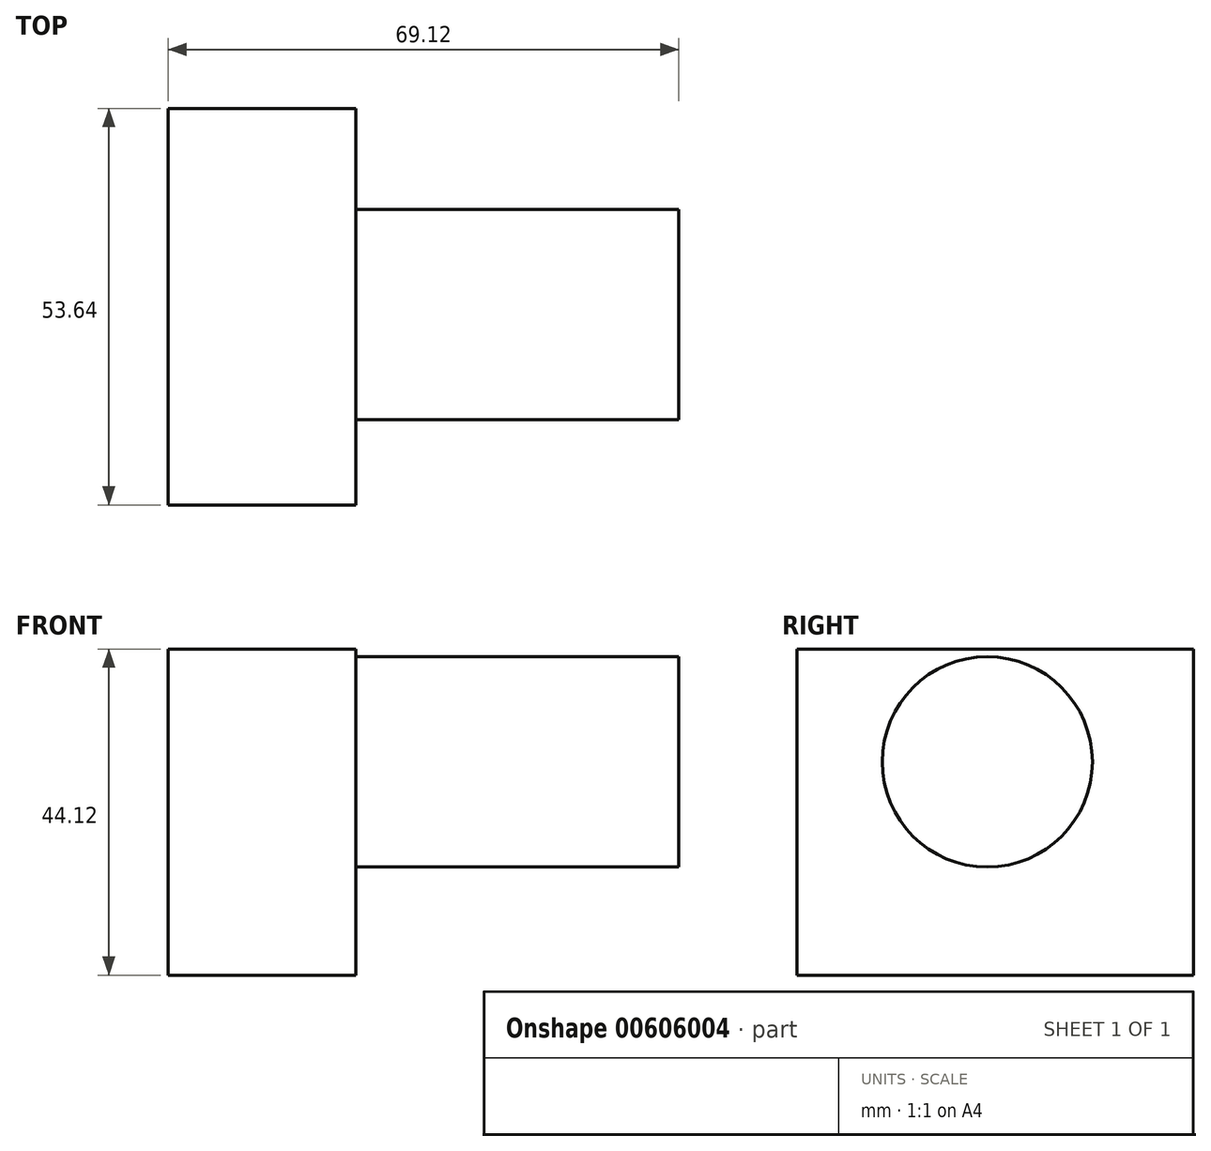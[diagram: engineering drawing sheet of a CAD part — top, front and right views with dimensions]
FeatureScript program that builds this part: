
annotation { "Feature Type Name" : "Feature", "Feature Type Description" : "" }
export const myFeature = defineFeature(function(context is Context, id is Id, definition is map)
    precondition{}
    {
        {
            var Q0;
            Q0=qCreatedBy(makeId("Right.planeOp"),FACE);
            var sketch = newSketch(context, id + "F0", { "sketchPlane" : qUnion([Q0])});
            skLineSegment(sketch, "E0.bottom", {"start": v(-35.96, 0) * mm, "end": v(17.68, 0) * mm});
            skLineSegment(sketch, "E0.top", {"start": v(-35.96, -44.12) * mm, "end": v(17.68, -44.12) * mm});
            skLineSegment(sketch, "E0.left", {"start": v(-35.96, 0) * mm, "end": v(-35.96, -44.12) * mm});
            skLineSegment(sketch, "E0.right", {"start": v(17.68, 0) * mm, "end": v(17.68, -44.12) * mm});
            skSolve(sketch);
        }
        {
            var Q0;
            Q0=makeQuery(id+"F0.imprint","IMPRINT",FACE,{"disambiguationData":[TD([[makeQuery(id+"F0.imprint","IMPRINT",EDGE,{"derivedFrom":sQuery(id+"F0.wireOp",EDGE,"E0.bottom")}),-1.0]])]});
            extrude(context, id + "F1", {"entities" : qUnion([Q0]), "depth" : 25.4 * mm, "offsetDistance" : 25.4 * mm});
        }
        {
            var Q0;
            Q0=makeQuery(id+"F1.opExtrude","CAP_FACE",FACE,{"disambiguationData":[OSD([sQuery(id+"F0.wireOp",EDGE,"E0.bottom"),sQuery(id+"F0.wireOp",EDGE,"E0.top"),sQuery(id+"F0.wireOp",EDGE,"E0.left"),sQuery(id+"F0.wireOp",EDGE,"E0.right")])],"isStart":false});
            var sketch = newSketch(context, id + "F2", { "sketchPlane" : qUnion([Q0])});
            skCircle(sketch, "E1", {"center": v(-10.21, -15.27) * mm, "radius": 14.23 * mm});
            skSolve(sketch);
        }
        {
            var Q0;
            Q0=makeQuery(id+"F2.imprint","IMPRINT",FACE,{"disambiguationData":[TD([[makeQuery(id+"F2.imprint","IMPRINT",EDGE,{"derivedFrom":sQuery(id+"F2.wireOp",EDGE,"E1")}),1.0]])]});
            extrude(context, id + "F3", {"entities" : qUnion([Q0]), "operationType" : NewBodyOperationType.ADD, "depth" : 43.72 * mm, "offsetDistance" : 25.4 * mm});
        }
    });
